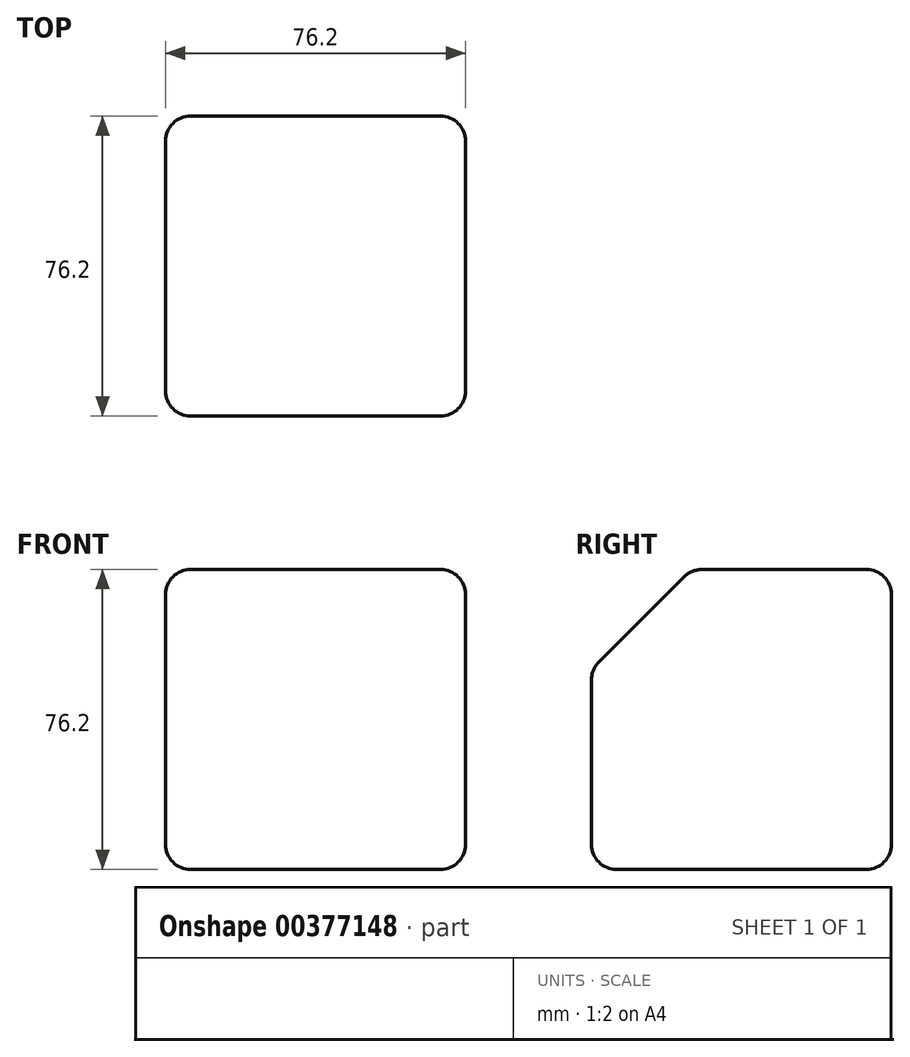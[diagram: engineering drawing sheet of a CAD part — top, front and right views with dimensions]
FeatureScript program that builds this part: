
annotation { "Feature Type Name" : "Feature", "Feature Type Description" : "" }
export const myFeature = defineFeature(function(context is Context, id is Id, definition is map)
    precondition{}
    {
        {
            var Q0;
            Q0=qCreatedBy(makeId("Top.planeOp"),FACE);
            var sketch = newSketch(context, id + "F0", { "sketchPlane" : qUnion([Q0])});
            skLineSegment(sketch, "E0.bottom", {"start": v(-38.1, 38.1) * mm, "end": v(38.1, 38.1) * mm});
            skLineSegment(sketch, "E0.top", {"start": v(-38.1, -38.1) * mm, "end": v(38.1, -38.1) * mm});
            skLineSegment(sketch, "E0.left", {"start": v(-38.1, 38.1) * mm, "end": v(-38.1, -38.1) * mm});
            skLineSegment(sketch, "E0.right", {"start": v(38.1, 38.1) * mm, "end": v(38.1, -38.1) * mm});
            skSolve(sketch);
        }
        {
            var Q0;
            Q0=makeQuery(id+"F0.imprint","IMPRINT",FACE,{"disambiguationData":[TD([[makeQuery(id+"F0.imprint","IMPRINT",EDGE,{"derivedFrom":sQuery(id+"F0.wireOp",EDGE,"E0.bottom")}),-1.0]])]});
            extrude(context, id + "F1", {"entities" : qUnion([Q0]), "depth" : 76.2 * mm});
        }
        {
            var Q0;
            Q0=makeQuery(id+"F1.opExtrude","CAP_EDGE",EDGE,{"disambiguationData":[OSD([sQuery(id+"F0.wireOp",EDGE,"E0.top")])],"isStart":false});
            chamfer(context, id + "F2", {"entities" : qUnion([Q0]), "width" : 25.4 * mm, "tangentPropagation" : true});
        }
        {
            var Q0;
            Q0=makeQuery(id+"F1.opExtrude","CAP_EDGE",EDGE,{"disambiguationData":[OSD([sQuery(id+"F0.wireOp",EDGE,"E0.right")])],"isStart":false});
            var Q1;
            Q1=makeQuery(id+"F1.opExtrude","CAP_EDGE",EDGE,{"disambiguationData":[OSD([sQuery(id+"F0.wireOp",EDGE,"E0.bottom")])],"isStart":false});
            var Q2;
            {var subQ0=sQuery(id+"F0.wireOp",EDGE,"E0.top");Q2=makeQuery(id+"F2.opChamfer","BLEND_EDGE",EDGE,{"blendedFrom":[makeQuery(id+"F1.opExtrude","CAP_EDGE",EDGE,{"disambiguationData":[OSD([subQ0])],"isStart":false}),makeQuery(id+"F1.opExtrude","CAP_FACE",FACE,{"disambiguationData":[OSD([sQuery(id+"F0.wireOp",EDGE,"E0.bottom"),subQ0,sQuery(id+"F0.wireOp",EDGE,"E0.left"),sQuery(id+"F0.wireOp",EDGE,"E0.right")])],"isStart":false})],"blendedInto":[makeQuery(id+"F1.opExtrude","CAP_FACE",FACE,{"disambiguationData":[OSD([sQuery(id+"F0.wireOp",EDGE,"E0.bottom"),subQ0,sQuery(id+"F0.wireOp",EDGE,"E0.left"),sQuery(id+"F0.wireOp",EDGE,"E0.right")])],"isStart":false})]});}
            var Q3;
            Q3=makeQuery(id+"F1.opExtrude","CAP_EDGE",EDGE,{"disambiguationData":[OSD([sQuery(id+"F0.wireOp",EDGE,"E0.left")])],"isStart":false});
            var Q4;
            Q4=makeQuery(id+"F1.opExtrude","SWEPT_EDGE",EDGE,{"disambiguationData":[OSD([sQuery(id+"F0.wireOp",EDGE,"E0.top"),sQuery(id+"F0.wireOp",EDGE,"E0.right")])]});
            var Q5;
            Q5=makeQuery(id+"F1.opExtrude","CAP_EDGE",EDGE,{"disambiguationData":[OSD([sQuery(id+"F0.wireOp",EDGE,"E0.right")])],"isStart":true});
            var Q6;
            Q6=makeQuery(id+"F1.opExtrude","SWEPT_EDGE",EDGE,{"disambiguationData":[OSD([sQuery(id+"F0.wireOp",EDGE,"E0.bottom"),sQuery(id+"F0.wireOp",EDGE,"E0.right")])]});
            var Q7;
            {var subQ0=sQuery(id+"F0.wireOp",EDGE,"E0.top");Q7=makeQuery(id+"F2.opChamfer","BLEND_EDGE",EDGE,{"blendedFrom":[makeQuery(id+"F1.opExtrude","CAP_EDGE",EDGE,{"disambiguationData":[OSD([subQ0])],"isStart":false}),makeQuery(id+"F1.opExtrude","SWEPT_FACE",FACE,{"disambiguationData":[OSD([subQ0])]})],"blendedInto":[makeQuery(id+"F1.opExtrude","SWEPT_FACE",FACE,{"disambiguationData":[OSD([subQ0])]})]});}
            var Q8;
            Q8=makeQuery(id+"F2.opChamfer","BLEND_EDGE",EDGE,{"blendedFrom":[makeQuery(id+"F1.opExtrude","CAP_EDGE",EDGE,{"disambiguationData":[OSD([sQuery(id+"F0.wireOp",EDGE,"E0.top")])],"isStart":false}),makeQuery(id+"F1.opExtrude","SWEPT_FACE",FACE,{"disambiguationData":[OSD([sQuery(id+"F0.wireOp",EDGE,"E0.right")])]})],"blendedInto":[makeQuery(id+"F1.opExtrude","SWEPT_FACE",FACE,{"disambiguationData":[OSD([sQuery(id+"F0.wireOp",EDGE,"E0.right")])]})]});
            var Q9;
            Q9=makeQuery(id+"F2.opChamfer","BLEND_EDGE",EDGE,{"blendedFrom":[makeQuery(id+"F1.opExtrude","CAP_EDGE",EDGE,{"disambiguationData":[OSD([sQuery(id+"F0.wireOp",EDGE,"E0.top")])],"isStart":false}),makeQuery(id+"F1.opExtrude","SWEPT_FACE",FACE,{"disambiguationData":[OSD([sQuery(id+"F0.wireOp",EDGE,"E0.left")])]})],"blendedInto":[makeQuery(id+"F1.opExtrude","SWEPT_FACE",FACE,{"disambiguationData":[OSD([sQuery(id+"F0.wireOp",EDGE,"E0.left")])]})]});
            var Q10;
            Q10=makeQuery(id+"F1.opExtrude","CAP_EDGE",EDGE,{"disambiguationData":[OSD([sQuery(id+"F0.wireOp",EDGE,"E0.top")])],"isStart":true});
            var Q11;
            Q11=makeQuery(id+"F1.opExtrude","SWEPT_EDGE",EDGE,{"disambiguationData":[OSD([sQuery(id+"F0.wireOp",EDGE,"E0.top"),sQuery(id+"F0.wireOp",EDGE,"E0.left")])]});
            var Q12;
            Q12=makeQuery(id+"F1.opExtrude","CAP_EDGE",EDGE,{"disambiguationData":[OSD([sQuery(id+"F0.wireOp",EDGE,"E0.left")])],"isStart":true});
            var Q13;
            Q13=makeQuery(id+"F1.opExtrude","CAP_EDGE",EDGE,{"disambiguationData":[OSD([sQuery(id+"F0.wireOp",EDGE,"E0.bottom")])],"isStart":true});
            var Q14;
            Q14=makeQuery(id+"F1.opExtrude","SWEPT_EDGE",EDGE,{"disambiguationData":[OSD([sQuery(id+"F0.wireOp",EDGE,"E0.bottom"),sQuery(id+"F0.wireOp",EDGE,"E0.left")])]});
            fillet(context, id + "F3", {"entities" : qUnion([Q0, Q1, Q2, Q3, Q4, Q5, Q6, Q7, Q8, Q9, Q10, Q11, Q12, Q13, Q14]), "radius" : 6.35 * mm, "tangentPropagation" : true, "allowEdgeOverflow" : false});
        }
    });
